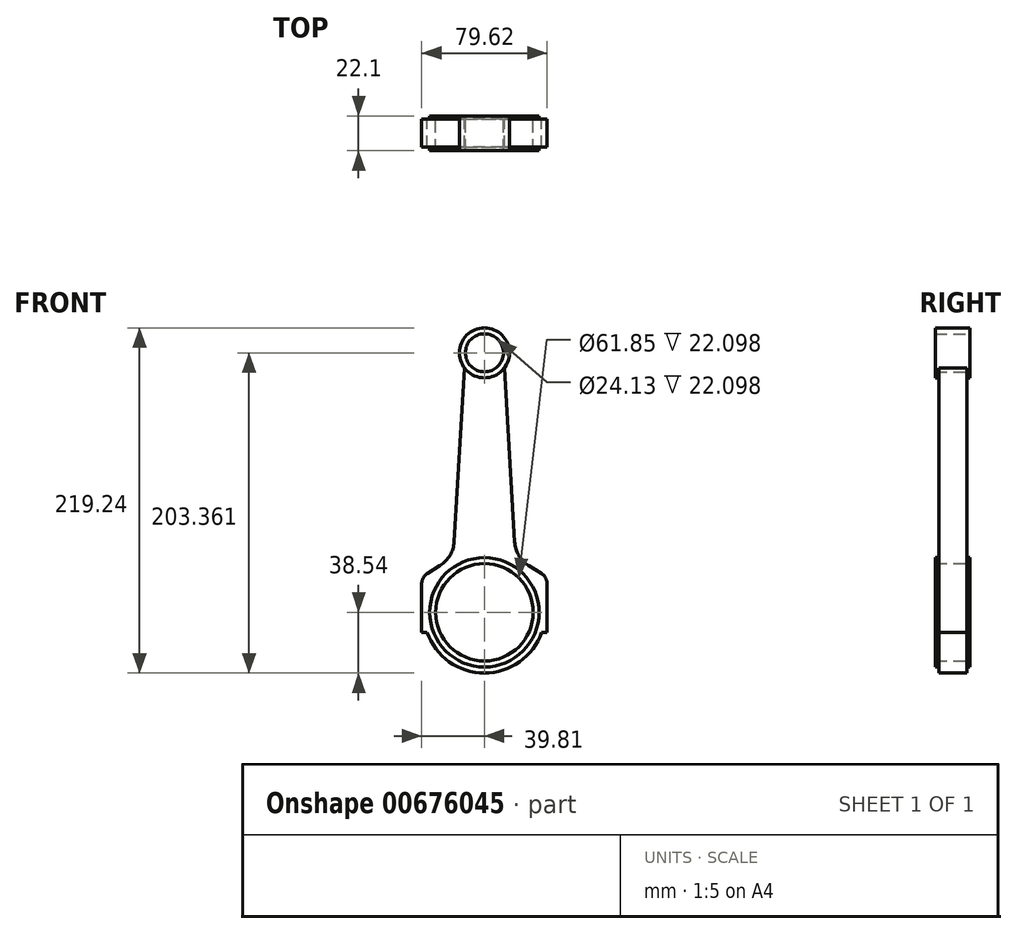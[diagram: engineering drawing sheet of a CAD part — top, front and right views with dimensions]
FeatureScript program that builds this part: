
annotation { "Feature Type Name" : "Feature", "Feature Type Description" : "" }
export const myFeature = defineFeature(function(context is Context, id is Id, definition is map)
    precondition{}
    {
        {
            var Q0;
            Q0=qCreatedBy(makeId("Front.planeOp"),FACE);
            var sketch = newSketch(context, id + "F0", { "sketchPlane" : qUnion([Q0])});
            skCircle(sketch, "E0", {"center": v(0, 0) * mm, "radius": 30.92 * mm});
            skLineSegment(sketch, "E1", {"start": v(0, 0) * mm, "end": v(0, 164.82) * mm, "construction": true});
            skCircle(sketch, "E2", {"center": v(0, 164.82) * mm, "radius": 12.07 * mm});
            skCircle(sketch, "E3.0", {"center": v(0, 164.82) * mm, "radius": 15.88 * mm});
            skLineSegment(sketch, "E4", {"start": v(-30.92, 0) * mm, "end": v(30.92, 0) * mm});
            skLineSegment(sketch, "E5", {"start": v(30.92, 0) * mm, "end": v(39.81, 0) * mm});
            skLineSegment(sketch, "E6", {"start": v(39.81, 0) * mm, "end": v(39.81, 18.17) * mm});
            skLineSegment(sketch, "E7", {"start": v(36.27, 24.61) * mm, "end": v(28.06, 29.8) * mm});
            skLineSegment(sketch, "E8", {"start": v(19.23, 44.77) * mm, "end": v(12.66, 155.24) * mm});
            skCircle(sketch, "E9.0", {"center": v(0, 0) * mm, "radius": 34.73 * mm});
            skArc(sketch, "E10", {"start": v(-36.4, -12.7) * mm, "mid": v(0, -38.54) * mm, "end": v(36.4, -12.7) * mm});
            skLineSegment(sketch, "E11.MirrorCS", {"start": v(-19.23, 44.77) * mm, "end": v(-12.66, 155.24) * mm});
            skLineSegment(sketch, "E12.MirrorCS", {"start": v(-36.27, 24.61) * mm, "end": v(-28.06, 29.8) * mm});
            skLineSegment(sketch, "E13.MirrorCS", {"start": v(-39.81, 0) * mm, "end": v(-39.81, 18.17) * mm});
            skLineSegment(sketch, "E14.MirrorCS", {"start": v(-30.92, 0) * mm, "end": v(-39.81, 0) * mm});
            skLineSegment(sketch, "E15", {"start": v(39.81, 0) * mm, "end": v(39.81, -12.7) * mm});
            skLineSegment(sketch, "E16", {"start": v(39.81, -12.7) * mm, "end": v(36.4, -12.7) * mm});
            skLineSegment(sketch, "E17.MirrorCS", {"start": v(-39.81, 0) * mm, "end": v(-39.81, -12.7) * mm});
            skLineSegment(sketch, "E18.MirrorCS", {"start": v(-39.81, -12.7) * mm, "end": v(-36.4, -12.7) * mm});
            skPoint(sketch, "E19.orphan", {"position": v(-12.04, 165.54) * mm});
            skPoint(sketch, "E20.orphan", {"position": v(12.04, 165.54) * mm});
            skPoint(sketch, "E21.visualSharp", {"position": v(-19.8, 35.03) * mm});
            skArc(sketch, "E21.filletArc", {"start": v(-28.06, 29.8) * mm, "mid": v(-21.84, 36.23) * mm, "end": v(-19.23, 44.77) * mm});
            skPoint(sketch, "E22.visualSharp", {"position": v(19.8, 35.03) * mm});
            skArc(sketch, "E22.filletArc", {"start": v(19.23, 44.77) * mm, "mid": v(21.84, 36.23) * mm, "end": v(28.06, 29.8) * mm});
            skPoint(sketch, "E23.visualSharp", {"position": v(-39.81, 22.37) * mm});
            skArc(sketch, "E23.filletArc", {"start": v(-36.27, 24.61) * mm, "mid": v(-38.87, 21.85) * mm, "end": v(-39.81, 18.17) * mm});
            skPoint(sketch, "E24.visualSharp", {"position": v(39.81, 22.37) * mm});
            skArc(sketch, "E24.filletArc", {"start": v(39.81, 18.17) * mm, "mid": v(38.87, 21.85) * mm, "end": v(36.27, 24.61) * mm});
            skSolve(sketch);
        }
        {
            var Q0;
            {var subQ4=sQuery(id+"F0.wireOp",EDGE,"E5");var subQ6=sQuery(id+"F0.wireOp",EDGE,"E9.0");var subQ7=makeQuery(id+"F0.imprint","INTERSECT",VERTEX,{"derivedFrom":[subQ4,subQ6]});Q0=makeQuery(id+"F0.imprint","IMPRINT",FACE,{"disambiguationData":[TD([[makeQuery(id+"F0.imprint","IMPRINT",EDGE,{"disambiguationData":[TD([[subQ7,-1.0]])],"derivedFrom":subQ6}),1.0]])]});}
            extrude(context, id + "F1", {"entities" : qUnion([Q0]), "endBound" : BoundingType.SYMMETRIC, "depth" : 22.1 * mm, "offsetDistance" : 25.4 * mm});
        }
        {
            var Q0;
            {var subQ9=sQuery(id+"F0.wireOp",EDGE,"E6");Q0=makeQuery(id+"F0.imprint","IMPRINT",FACE,{"disambiguationData":[TD([[makeQuery(id+"F0.imprint","IMPRINT",EDGE,{"derivedFrom":subQ9}),1.0]])]});}
            extrude(context, id + "F2", {"entities" : qUnion([Q0]), "operationType" : NewBodyOperationType.ADD, "endBound" : BoundingType.SYMMETRIC, "depth" : 17.78 * mm, "offsetDistance" : 25.4 * mm});
        }
        {
            var Q0;
            Q0=makeQuery(id+"F0.imprint","IMPRINT",FACE,{"disambiguationData":[TD([[makeQuery(id+"F0.imprint","IMPRINT",EDGE,{"derivedFrom":sQuery(id+"F0.wireOp",EDGE,"E2")}),-1.0]])]});
            extrude(context, id + "F3", {"entities" : qUnion([Q0]), "operationType" : NewBodyOperationType.ADD, "endBound" : BoundingType.SYMMETRIC, "depth" : 22.1 * mm, "offsetDistance" : 25.4 * mm});
        }
        {
            var Q0;
            {var subQ4=sQuery(id+"F0.wireOp",EDGE,"E5");var subQ6=sQuery(id+"F0.wireOp",EDGE,"E9.0");var subQ7=makeQuery(id+"F0.imprint","INTERSECT",VERTEX,{"derivedFrom":[subQ4,subQ6]});Q0=makeQuery(id+"F0.imprint","IMPRINT",FACE,{"disambiguationData":[TD([[makeQuery(id+"F0.imprint","IMPRINT",EDGE,{"disambiguationData":[TD([[subQ7,1.0]])],"derivedFrom":subQ6}),1.0]])]});}
            extrude(context, id + "F4", {"entities" : qUnion([Q0]), "endBound" : BoundingType.SYMMETRIC, "depth" : 22.1 * mm, "offsetDistance" : 25.4 * mm});
        }
        {
            var Q0;
            Q0=makeQuery(id+"F0.imprint","IMPRINT",FACE,{"disambiguationData":[TD([[makeQuery(id+"F0.imprint","IMPRINT",EDGE,{"derivedFrom":sQuery(id+"F0.wireOp",EDGE,"E10")}),1.0]])]});
            extrude(context, id + "F5", {"entities" : qUnion([Q0]), "operationType" : NewBodyOperationType.ADD, "endBound" : BoundingType.SYMMETRIC, "depth" : 17.78 * mm, "offsetDistance" : 25.4 * mm});
        }
    });
